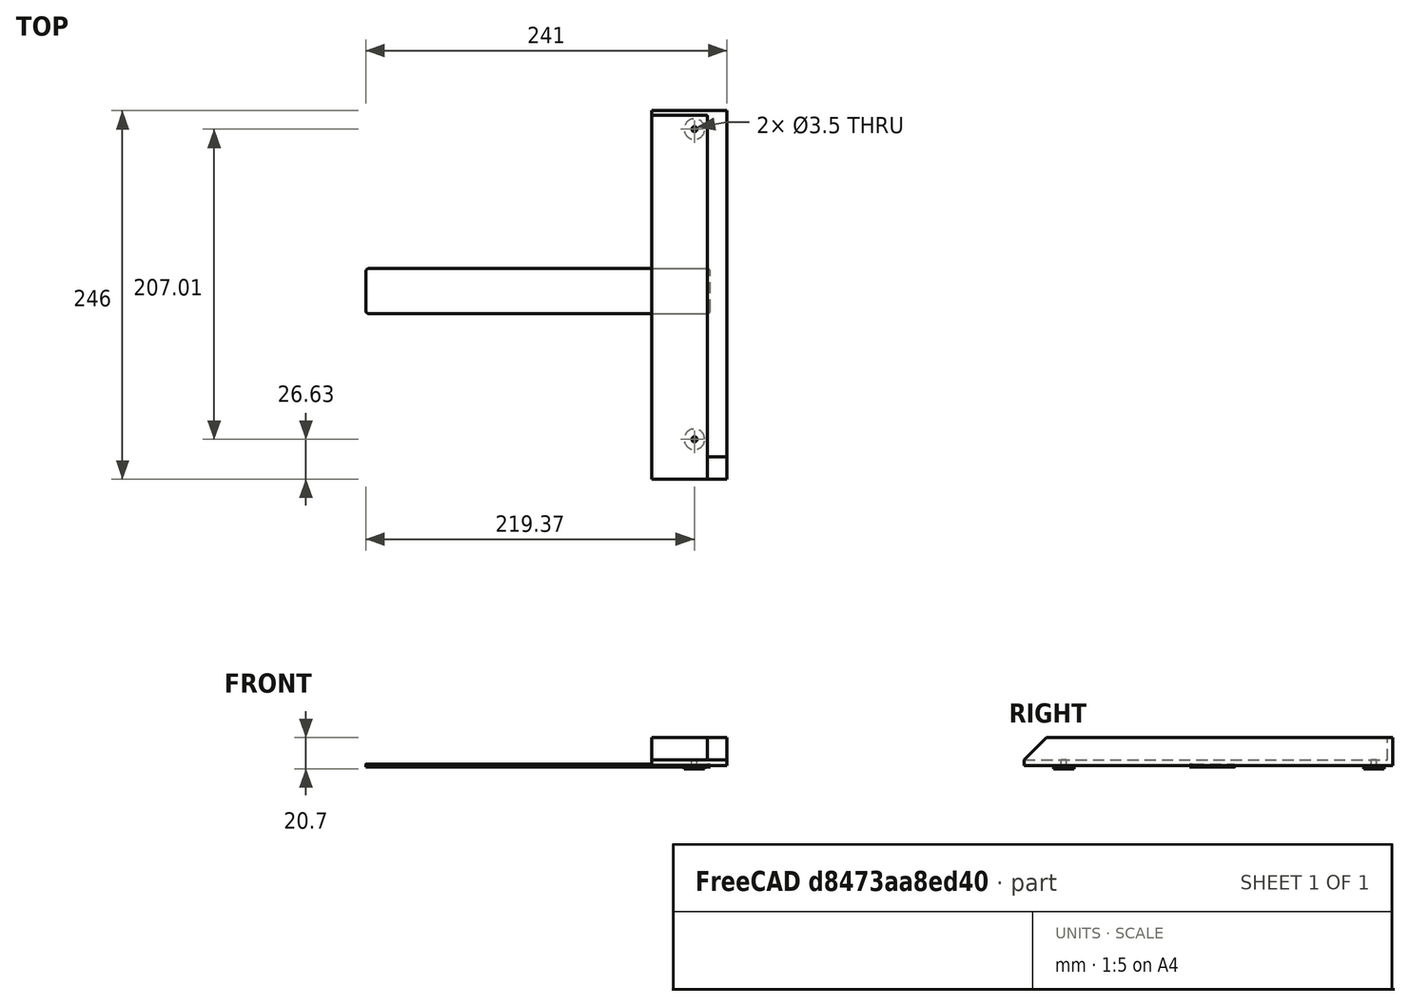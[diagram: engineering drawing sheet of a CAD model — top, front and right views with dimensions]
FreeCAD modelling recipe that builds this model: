
FCSTD DOCUMENT  (FreeCAD 0.18R16110 (Git))
Label: Anet_A8_removable_heat_bed
License: All rights reserved
LicenseURL: http://en.wikipedia.org/wiki/All_rights_reserved
objects: Part::Box×5, Part::Cut×4, Part::Cylinder×4, Part::MultiFuse×3, Part::Fillet×1, Part::Mirroring×1, App::Part×1
note: 18 computed .brp shape members not serialized (recipe doc carries the construction recipe); baked Part::Feature solids carry a one-line shape summary decoded from their .brp

FEATURE [Part::Box] Box  label="Cube"
  AttacherType = Attacher::AttachEngine3D
  Height = 2
  Length = 230
  Width = 30
FEATURE [Part::Fillet] Fillet
  Base = -> Box
  Edges = 4 edges r=2: [Edge1,Edge3,Edge5,Edge7]
  Placement = pos=(11,110.55,-1) rot=(0,0,1;0rad)
FEATURE [Part::Box] Box001  label="Cube001"
  AttacherType = Attacher::AttachEngine3D
  Height = 3.75
  Length = 50
  Width = 246
FEATURE [Part::Box] Box002  label="Cube002"
  AttacherType = Attacher::AttachEngine3D
  Height = 14.95
  Length = 50
  Placement = pos=(0,0,3.75) rot=(0,0,1;0rad)
  Width = 246
FEATURE [Part::Box] Box003  label="Cube003"
  AttacherType = Attacher::AttachEngine3D
  Height = 14.95
  Length = 37.15
  Placement = pos=(12.85,0,3.75) rot=(0,0,1;0rad)
  Width = 242.75
FEATURE [Part::Cut] Cut
  Base = -> Box002
  Tool = -> Box003
FEATURE [Part::Box] Box004  label="Cube004"
  AttacherType = Attacher::AttachEngine3D
  Height = 28
  Length = 20
  Placement = pos=(0,-14.1422,17.8921) rot=(-1,0,0;0.785398rad)
  Width = 20
FEATURE [Part::Cut] Cut001
  Base = -> Cut
  Tool = -> Box004
FEATURE [Part::MultiFuse] Fusion
  Shapes = -> [Box001,Cut001]
FEATURE [Part::Cylinder] Cylinder
  Angle = 360
  AttacherType = Attacher::AttachEngine3D
  Height = 2
  Placement = pos=(21.63,26.63,-2) rot=(0,0,1;0rad)
  Radius = 6.88
FEATURE [Part::Cylinder] Cylinder001
  Angle = 360
  AttacherType = Attacher::AttachEngine3D
  Height = 2
  Placement = pos=(21.63,233.64,-2) rot=(0,0,1;0rad)
  Radius = 6.88
FEATURE [Part::Cylinder] Cylinder002
  Angle = 360
  AttacherType = Attacher::AttachEngine3D
  Height = 6
  Placement = pos=(21.63,26.63,-2) rot=(0,0,1;0rad)
  Radius = 1.75
FEATURE [Part::MultiFuse] Fusion001
  Shapes = -> [Cylinder,Fusion]
FEATURE [Part::Cut] Cut002
  Base = -> Fusion001
  Tool = -> Cylinder002
FEATURE [Part::Cylinder] Cylinder003
  Angle = 360
  AttacherType = Attacher::AttachEngine3D
  Height = 6
  Placement = pos=(21.63,233.64,-2) rot=(0,0,1;0rad)
  Radius = 1.75
FEATURE [Part::MultiFuse] Fusion002
  Shapes = -> [Cut002,Cylinder001]
FEATURE [Part::Cut] Cut003
  Base = -> Fusion002
  Tool = -> Cylinder003
FEATURE [Part::Mirroring] Part__Mirroring  label="Cut003 (Mirror #1)"
  Base = (126,0,0)
  Normal = (1,0,0)
  Source = -> Cut003
FEATURE [App::Part] Part  label="Anet_A8_removable_heat_bed_support"
  Group = -> [Cut,Cut001,Fusion002,Cylinder003,Cut003,Cut002,Cylinder001,Box002,Box001,Cylinder002,Box003,Fusion001,Fusion,Box004,Cylinder,Part__Mirroring,Box,Fillet]
  Origin = -> Origin
